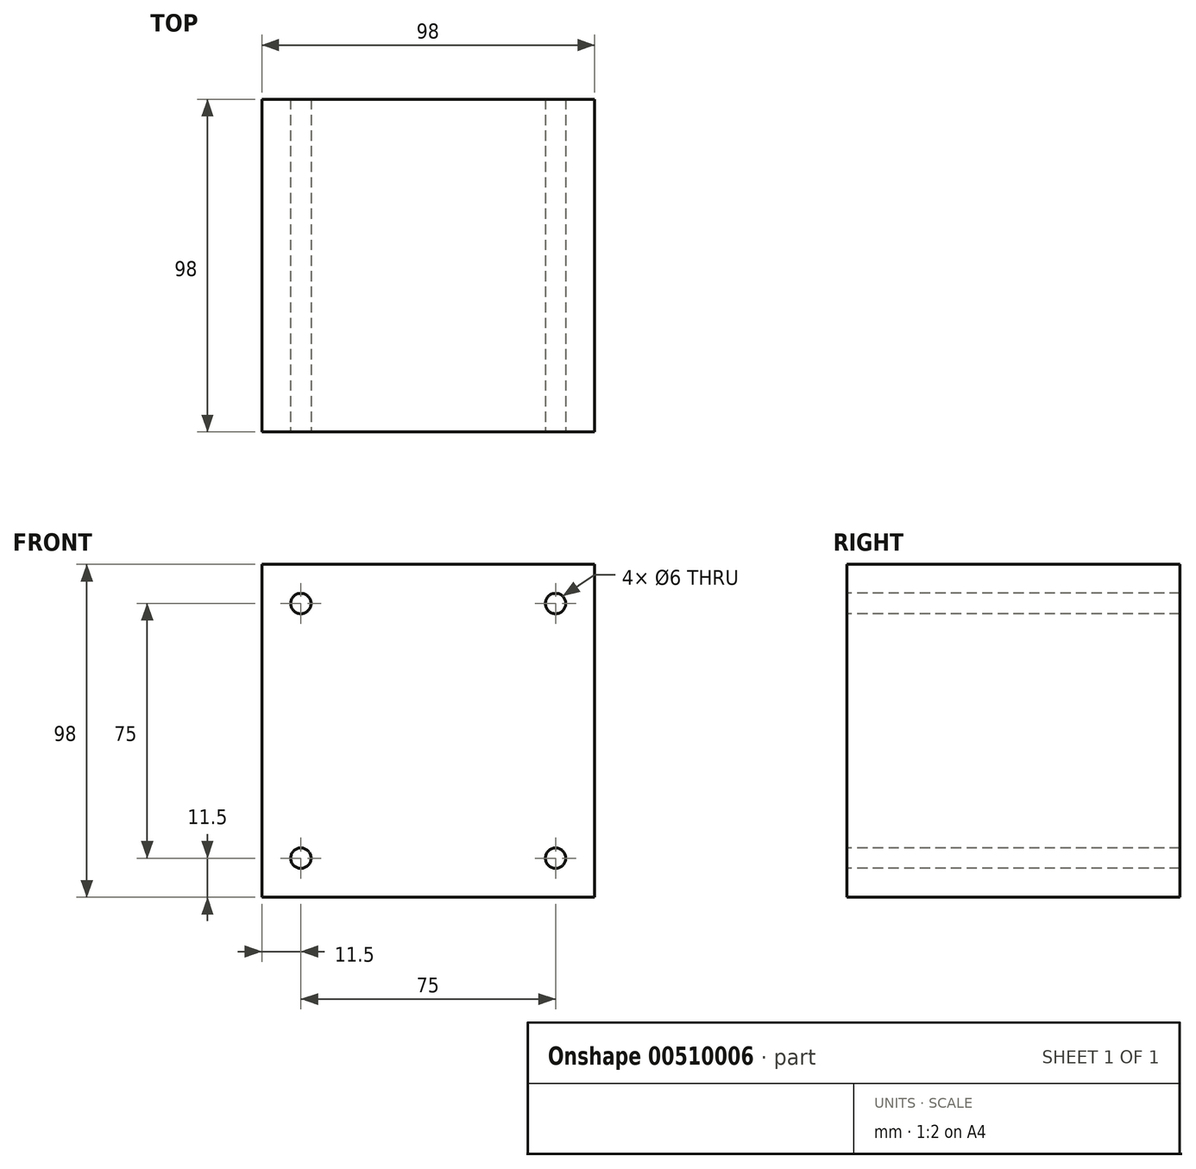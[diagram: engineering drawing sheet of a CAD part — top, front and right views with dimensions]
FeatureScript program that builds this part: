
annotation { "Feature Type Name" : "Feature", "Feature Type Description" : "" }
export const myFeature = defineFeature(function(context is Context, id is Id, definition is map)
    precondition{}
    {
        {
            var Q0;
            Q0=qCreatedBy(makeId("Front.planeOp"),FACE);
            var sketch = newSketch(context, id + "F0", { "sketchPlane" : qUnion([Q0])});
            skLineSegment(sketch, "E0.bottom", {"start": v(-49, -49) * mm, "end": v(49, -49) * mm});
            skLineSegment(sketch, "E0.top", {"start": v(-49, 49) * mm, "end": v(49, 49) * mm});
            skLineSegment(sketch, "E0.left", {"start": v(-49, -49) * mm, "end": v(-49, 49) * mm});
            skLineSegment(sketch, "E0.right", {"start": v(49, -49) * mm, "end": v(49, 49) * mm});
            skLineSegment(sketch, "E1", {"start": v(-49, 49) * mm, "end": v(49, -49) * mm, "construction": true});
            skSolve(sketch);
        }
        {
            var Q0;
            Q0 = qSketchRegion(id + "F0", true);
            extrude(context, id + "F1", {"entities" : qUnion([Q0]), "depth" : 98 * mm});
        }
        {
            var Q0;
            Q0=makeQuery(id+"F1.opExtrude","CAP_FACE",FACE,{"disambiguationData":[OSD([sQuery(id+"F0.wireOp",EDGE,"E0.bottom"),sQuery(id+"F0.wireOp",EDGE,"E0.top"),sQuery(id+"F0.wireOp",EDGE,"E0.left"),sQuery(id+"F0.wireOp",EDGE,"E0.right")])],"isStart":false});
            var sketch = newSketch(context, id + "F2", { "sketchPlane" : qUnion([Q0])});
            skLineSegment(sketch, "E2", {"start": v(-49, 49) * mm, "end": v(49, -49) * mm, "construction": true});
            skLineSegment(sketch, "E3.bottom", {"start": v(-37.5, 37.5) * mm, "end": v(37.5, 37.5) * mm, "construction": true});
            skLineSegment(sketch, "E3.top", {"start": v(-37.5, -37.5) * mm, "end": v(37.5, -37.5) * mm, "construction": true});
            skLineSegment(sketch, "E3.left", {"start": v(-37.5, 37.5) * mm, "end": v(-37.5, -37.5) * mm, "construction": true});
            skLineSegment(sketch, "E3.right", {"start": v(37.5, 37.5) * mm, "end": v(37.5, -37.5) * mm, "construction": true});
            skPoint(sketch, "E4", {"position": v(-37.5, 37.5) * mm});
            skPoint(sketch, "E5", {"position": v(37.5, -37.5) * mm});
            skPoint(sketch, "E6", {"position": v(37.5, 37.5) * mm});
            skPoint(sketch, "E7", {"position": v(-37.5, -37.5) * mm});
            skSolve(sketch);
        }
        {
            var Q0;
            Q0=sQuery(id+"F2.wireOp",VERTEX,"E4");
            var Q1;
            Q1=sQuery(id+"F2.wireOp",VERTEX,"E6");
            var Q2;
            Q2=sQuery(id+"F2.wireOp",VERTEX,"E5");
            var Q3;
            Q3=sQuery(id+"F2.wireOp",VERTEX,"E7");
            var Q4;
            Q4=makeQuery(id+"F1.opExtrude","SWEPT_BODY",BODY,{"disambiguationData":[OSD([sQuery(id+"F0.wireOp",EDGE,"E0.bottom"),sQuery(id+"F0.wireOp",EDGE,"E0.top"),sQuery(id+"F0.wireOp",EDGE,"E0.left"),sQuery(id+"F0.wireOp",EDGE,"E0.right")])]});
            hole(context, id + "F3", {"style" : HoleStyle.SIMPLE, "endStyle" : HoleEndStyle.THROUGH, "holeDiameter" : 6 * mm, "isTappedThrough" : true, "tappedDepth" : 12 * mm, "tapClearance" : 3, "locations" : qUnion([Q0, Q1, Q2, Q3]), "scope" : qUnion([Q4])});
        }
    });
